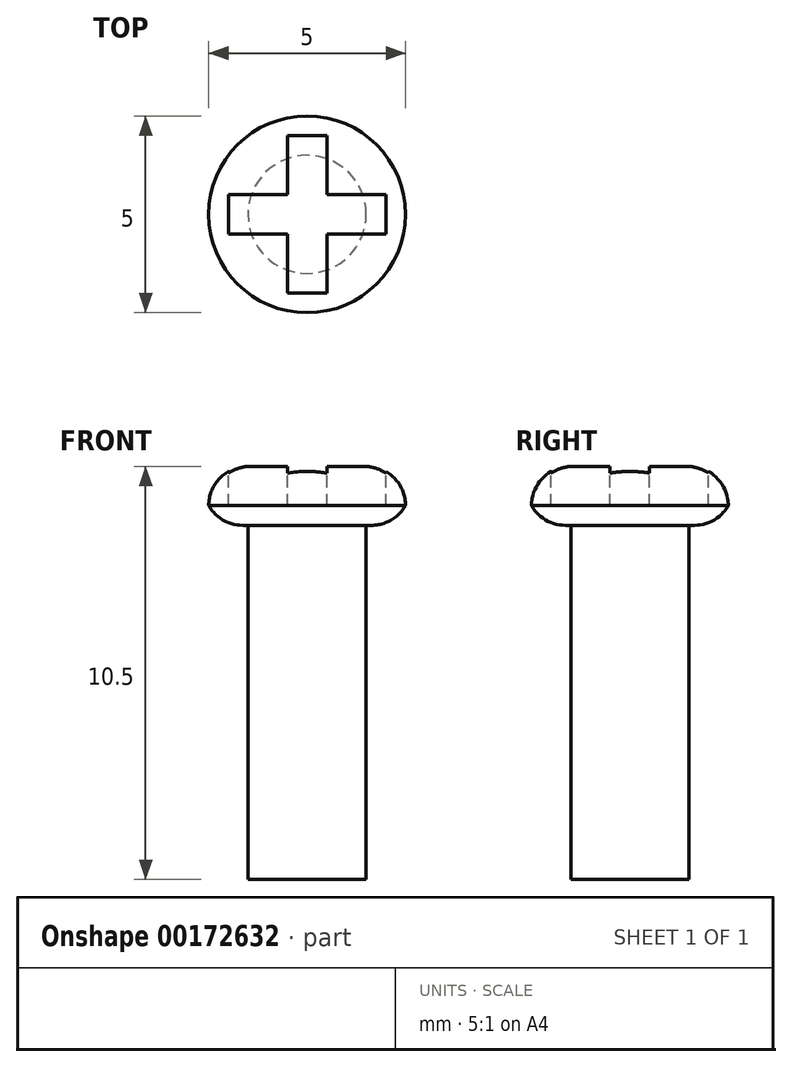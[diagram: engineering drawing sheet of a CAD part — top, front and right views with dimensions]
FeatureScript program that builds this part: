
annotation { "Feature Type Name" : "Feature", "Feature Type Description" : "" }
export const myFeature = defineFeature(function(context is Context, id is Id, definition is map)
    precondition{}
    {
        {
            var Q0;
            Q0=qCreatedBy(makeId("Top.planeOp"),FACE);
            var sketch = newSketch(context, id + "F0", { "sketchPlane" : qUnion([Q0])});
            skCircle(sketch, "E0", {"center": v(0, 0) * mm, "radius": 1.5 * mm});
            skSolve(sketch);
        }
        {
            var Q0;
            Q0=qSketchRegion(id+"F0",true);
            extrude(context, id + "F1", {"entities" : qUnion([Q0]), "depth" : 9 * mm});
        }
        {
            var Q0;
            Q0=makeQuery(id+"F1.opExtrude","CAP_FACE",FACE,{"disambiguationData":[OSD([sQuery(id+"F0.wireOp",EDGE,"E0")])],"isStart":false});
            var sketch = newSketch(context, id + "F2", { "sketchPlane" : qUnion([Q0])});
            skCircle(sketch, "E1", {"center": v(0, 0) * mm, "radius": 2.5 * mm});
            skSolve(sketch);
        }
        {
            var Q0;
            Q0=qSketchRegion(id+"F2",true);
            extrude(context, id + "F3", {"entities" : qUnion([Q0]), "operationType" : NewBodyOperationType.ADD, "depth" : 1.5 * mm});
        }
        {
            var Q0;
            Q0=makeQuery(id+"F3.opExtrude","CAP_FACE",FACE,{"disambiguationData":[OSD([sQuery(id+"F2.wireOp",EDGE,"E1")])],"isStart":false});
            var sketch = newSketch(context, id + "F4", { "sketchPlane" : qUnion([Q0])});
            skLineSegment(sketch, "E2.bottom", {"start": v(-0.5, 2) * mm, "end": v(0.5, 2) * mm});
            skLineSegment(sketch, "E2.top", {"start": v(-0.5, -2) * mm, "end": v(0.5, -2) * mm});
            skLineSegment(sketch, "E2.left", {"start": v(-0.5, 2) * mm, "end": v(-0.5, -2) * mm});
            skLineSegment(sketch, "E2.right", {"start": v(0.5, 2) * mm, "end": v(0.5, -2) * mm});
            skPoint(sketch, "E2.middle", {"position": v(0, 0) * mm});
            skLineSegment(sketch, "E3.bottom", {"start": v(-2, 0.5) * mm, "end": v(2, 0.5) * mm});
            skLineSegment(sketch, "E3.top", {"start": v(-2, -0.5) * mm, "end": v(2, -0.5) * mm});
            skLineSegment(sketch, "E3.left", {"start": v(-2, 0.5) * mm, "end": v(-2, -0.5) * mm});
            skLineSegment(sketch, "E3.right", {"start": v(2, 0.5) * mm, "end": v(2, -0.5) * mm});
            skSolve(sketch);
        }
        {
            var Q0;
            Q0=qSketchRegion(id+"F4",true);
            extrude(context, id + "F5", {"entities" : qUnion([Q0]), "operationType" : NewBodyOperationType.REMOVE, "oppositeDirection" : true, "depth" : 1 * mm});
        }
        {
            var Q0;
            Q0=makeQuery(id+"F3.opExtrude","CAP_EDGE",EDGE,{"disambiguationData":[OSD([sQuery(id+"F2.wireOp",EDGE,"E1")])],"isStart":false});
            fillet(context, id + "F6", {"entities" : qUnion([Q0]), "radius" : 1 * mm, "tangentPropagation" : true, "allowEdgeOverflow" : false});
        }
        {
            var Q0;
            Q0=makeQuery(id+"F3.opExtrude","CAP_EDGE",EDGE,{"disambiguationData":[OSD([sQuery(id+"F2.wireOp",EDGE,"E1")])],"isStart":true});
            fillet(context, id + "F7", {"entities" : qUnion([Q0]), "radius" : 1 * mm, "tangentPropagation" : true, "allowEdgeOverflow" : false});
        }
    });
